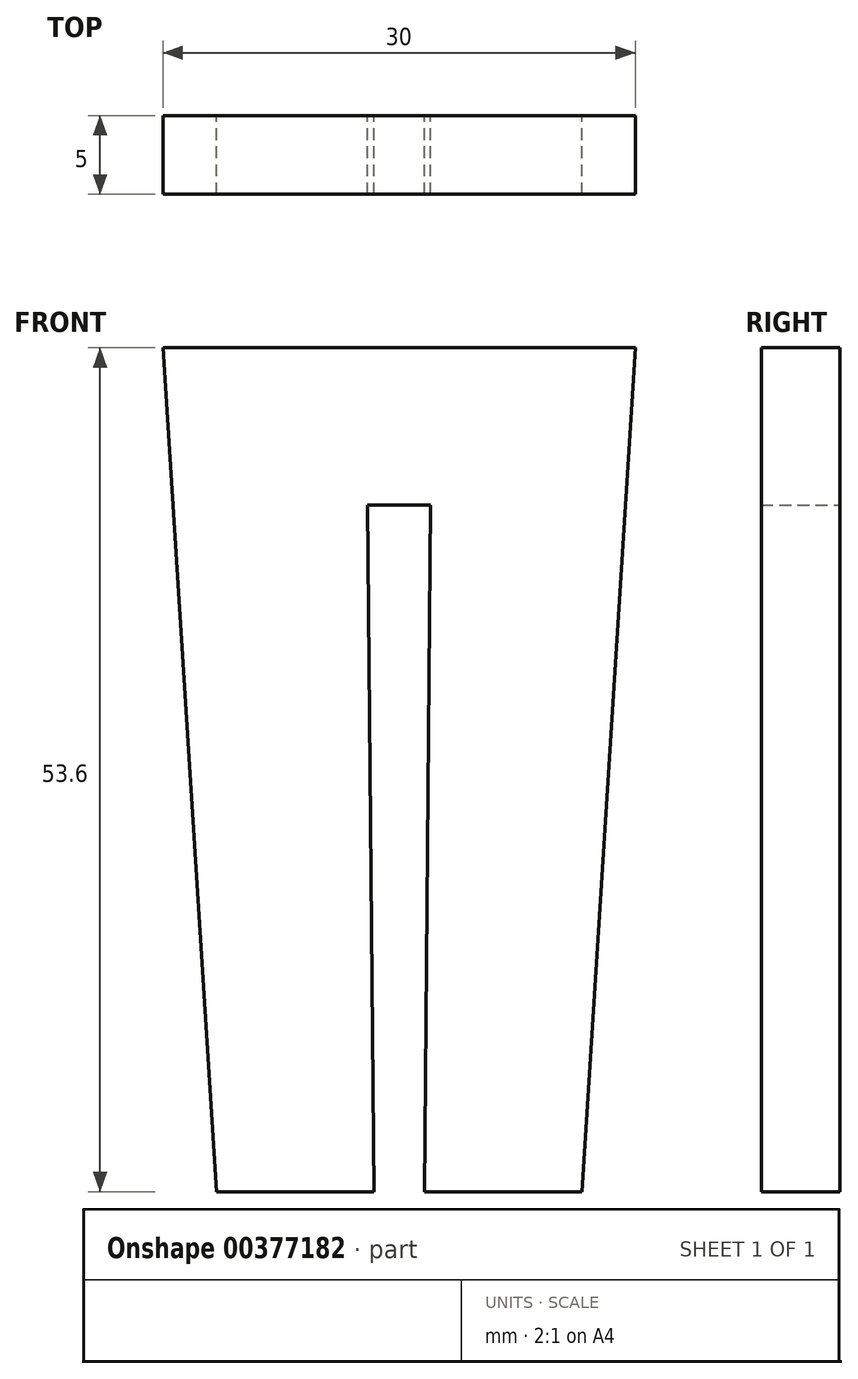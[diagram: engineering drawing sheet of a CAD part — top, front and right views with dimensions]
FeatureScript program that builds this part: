
annotation { "Feature Type Name" : "Feature", "Feature Type Description" : "" }
export const myFeature = defineFeature(function(context is Context, id is Id, definition is map)
    precondition{}
    {
        {
            var Q0;
            Q0=qCreatedBy(makeId("Front.planeOp"),FACE);
            var sketch = newSketch(context, id + "F0", { "sketchPlane" : qUnion([Q0])});
            skLineSegment(sketch, "E0", {"start": v(0, 0) * mm, "end": v(15, 0) * mm});
            skLineSegment(sketch, "E1", {"start": v(15, 0) * mm, "end": v(11.6, -53.6) * mm});
            skLineSegment(sketch, "E2", {"start": v(11.6, -53.6) * mm, "end": v(1.6, -53.6) * mm});
            skLineSegment(sketch, "E3", {"start": v(1.6, -53.6) * mm, "end": v(2, -10) * mm});
            skLineSegment(sketch, "E4", {"start": v(2, -10) * mm, "end": v(0, -10) * mm});
            skLineSegment(sketch, "E5.MirrorCS", {"start": v(-2, -10) * mm, "end": v(0, -10) * mm});
            skLineSegment(sketch, "E6.MirrorCS", {"start": v(-11.6, -53.6) * mm, "end": v(-1.6, -53.6) * mm});
            skLineSegment(sketch, "E7.MirrorCS", {"start": v(-1.6, -53.6) * mm, "end": v(-2, -10) * mm});
            skLineSegment(sketch, "E8.MirrorCS", {"start": v(-15, 0) * mm, "end": v(-11.6, -53.6) * mm});
            skLineSegment(sketch, "E9.MirrorCS", {"start": v(0, 0) * mm, "end": v(-15, 0) * mm});
            skSolve(sketch);
        }
        {
            var Q0;
            Q0=makeQuery(id+"F0.imprint","IMPRINT",FACE,{"disambiguationData":[TD([[makeQuery(id+"F0.imprint","IMPRINT",EDGE,{"derivedFrom":sQuery(id+"F0.wireOp",EDGE,"E0")}),-1.0]])]});
            extrude(context, id + "F1", {"entities" : qUnion([Q0]), "depth" : 5 * mm});
        }
    });
